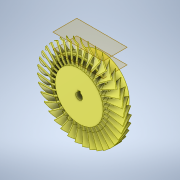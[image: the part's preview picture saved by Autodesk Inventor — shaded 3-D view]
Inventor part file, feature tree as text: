
AUTODESK INVENTOR PART (.ipt)
format: ipt  version: 2021.2 (Build 252289000, 289)  size: 4,587,520 bytes
history: native  units: in
note: dims shown in document units (in); Inventor stores cm internally (conversion verified against a paired STEP export)
features: sketch x6, extrude x4, plane x2, loft x1, pattern_circular x1, revolve x1, other x1
ambient origin geometry x8: Origin, YZ Plane, XZ Plane, XY Plane, X Axis, Y Axis, Z Axis, Center Point
bodies: Solid1 (feature_tree)
feature tree (16):
  extrude  "Extrusion1"  Depth=1.0in
  plane  "Work Plane1"
  extrude  "Extrusion2"  Depth=0.5in TaperAngle=0.0deg
  plane  "Work Plane2"
  sketch  "Sketch3"  dims[d7=2.0in d22=0.315in]
  extrude  "Extrusion3"  Depth=0.315in
  sketch  "Sketch6"  dims[d25=0.0in d26=0.0in]
  loft  "Loft2"
  pattern_circular  "Circular Pattern2"  Angle=90.0deg  [1 undecoded]
  revolve  "Revolution2"  Angle=90.0deg
  extrude  "Extrusion5"  Depth=0.0625in
  sketch  "Sketch1"  dims[d0=2.2in d1=1.0in d2=0.0777in]
  sketch  "Sketch2"  dims[d3=1.3in d5=0.5in d6=0.0in]
  sketch  "Sketch5"  dims[d23=0.125in d24=0.125in]
  other  "Edges2"
  sketch  "Sketch7"  dims[d27=3.9375in d30=0.0in d31=90.0deg d32=0.0in d33=90.0deg d35=0.0625in d36=0.5in d37=0.0312in d38=0.0625in d39=14.1732in d40=360.0deg d42=0.125in d43=0.5in d45=0.3in d46=0.0in d47=0.05in d48=90.0deg d49=0.0in d50=0.0in]
note: 1 required parameter value undecoded (feature->parameter linkage not recoverable at this tier; creation-order binding heuristic only, values carry confidence <= 0.55)
